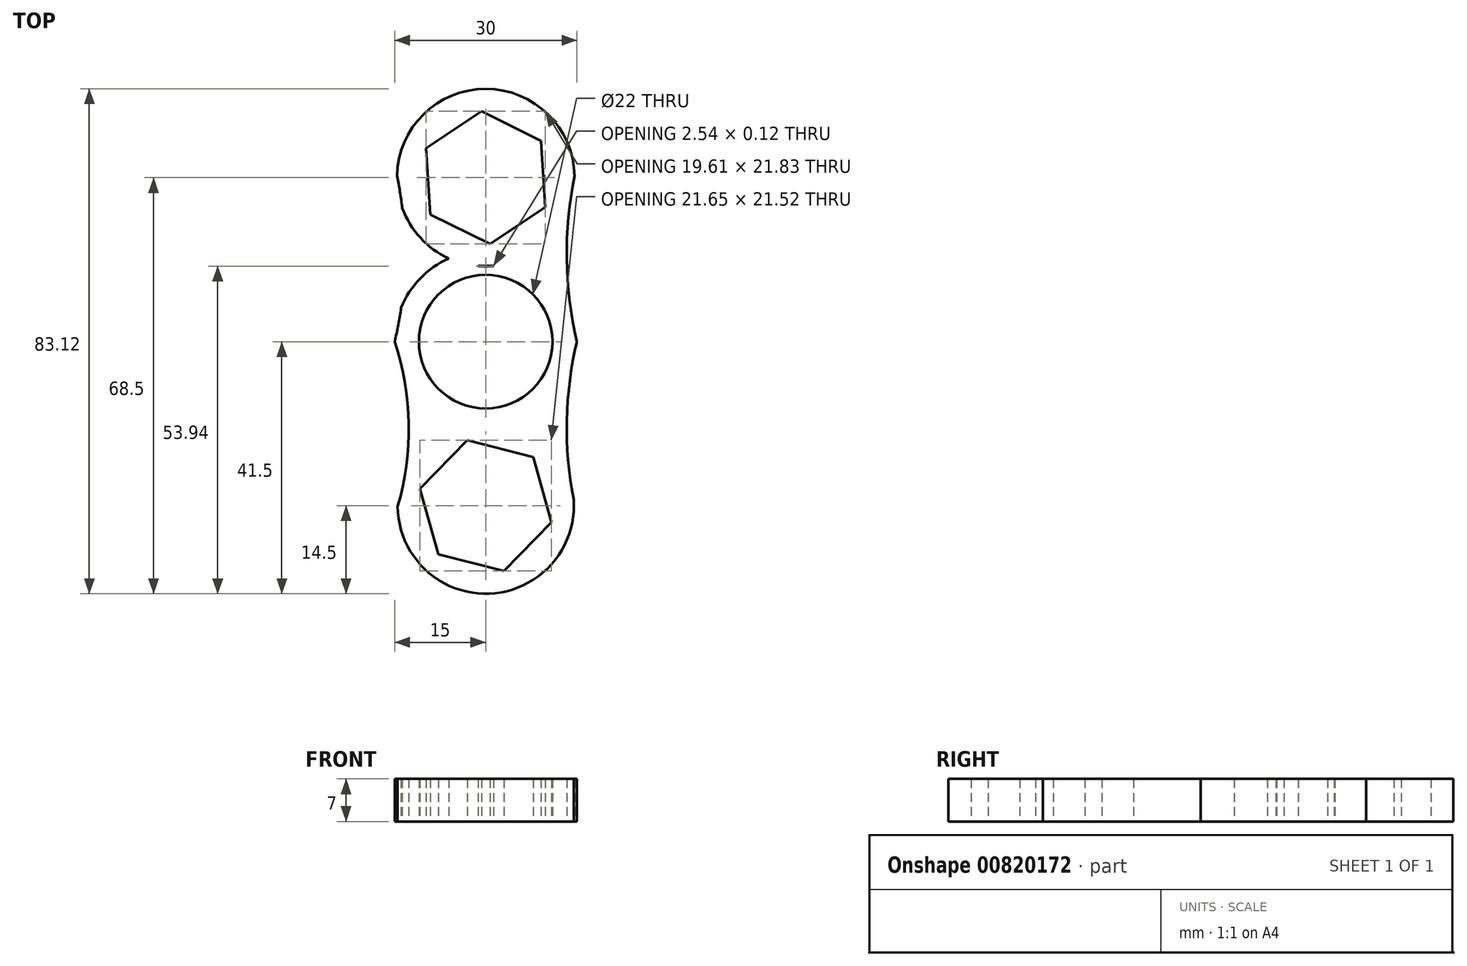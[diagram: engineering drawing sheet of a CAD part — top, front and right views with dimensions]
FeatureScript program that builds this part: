
annotation { "Feature Type Name" : "Feature", "Feature Type Description" : "" }
export const myFeature = defineFeature(function(context is Context, id is Id, definition is map)
    precondition{}
    {
        {
            var Q0;
            Q0=qCreatedBy(makeId("Top.planeOp"),FACE);
            var sketch = newSketch(context, id + "F0", { "sketchPlane" : qUnion([Q0])});
            skCircle(sketch, "E0", {"center": v(0, 0) * mm, "radius": 11 * mm});
            skCircle(sketch, "E1", {"center": v(0, 0) * mm, "radius": 12.5 * mm});
            skCircle(sketch, "E2", {"center": v(0, 27) * mm, "radius": 12 * mm});
            skCircle(sketch, "E3", {"center": v(0, -27) * mm, "radius": 12 * mm});
            skCircle(sketch, "E4", {"center": v(0, 27) * mm, "radius": 14.62 * mm});
            skCircle(sketch, "E5", {"center": v(0, 0) * mm, "radius": 15 * mm});
            skCircle(sketch, "E6", {"center": v(0, -27) * mm, "radius": 14.5 * mm});
            skCircle(sketch, "E7.cCircle", {"center": v(0, 27) * mm, "radius": 9.47 * mm, "construction": true});
            skLineSegment(sketch, "E7.0", {"start": v(9.8, 22.15) * mm, "end": v(0.7, 16.08) * mm});
            skLineSegment(sketch, "E7.1", {"start": v(0.7, 16.08) * mm, "end": v(-9.1, 20.94) * mm});
            skLineSegment(sketch, "E7.2", {"start": v(-9.1, 20.94) * mm, "end": v(-9.8, 31.85) * mm});
            skLineSegment(sketch, "E7.3", {"start": v(-9.8, 31.85) * mm, "end": v(-0.7, 37.92) * mm});
            skLineSegment(sketch, "E7.4", {"start": v(-0.7, 37.92) * mm, "end": v(9.1, 33.06) * mm});
            skLineSegment(sketch, "E7.5", {"start": v(9.1, 33.06) * mm, "end": v(9.8, 22.15) * mm});
            skPoint(sketch, "E7.0.midPoint", {"position": v(5.25, 19.11) * mm});
            skPoint(sketch, "E8.0.midPoint", {"position": v(5.25, -7.89) * mm});
            skCircle(sketch, "E9.cCircle", {"center": v(0, -27) * mm, "radius": 9.68 * mm, "construction": true});
            skLineSegment(sketch, "E9.0", {"start": v(10.82, -29.77) * mm, "end": v(3.01, -37.76) * mm});
            skLineSegment(sketch, "E9.1", {"start": v(3.01, -37.76) * mm, "end": v(-7.81, -34.99) * mm});
            skLineSegment(sketch, "E9.2", {"start": v(-7.81, -34.99) * mm, "end": v(-10.82, -24.23) * mm});
            skLineSegment(sketch, "E9.3", {"start": v(-10.82, -24.23) * mm, "end": v(-3.01, -16.24) * mm});
            skLineSegment(sketch, "E9.4", {"start": v(-3.01, -16.24) * mm, "end": v(7.81, -19.01) * mm});
            skLineSegment(sketch, "E9.5", {"start": v(7.81, -19.01) * mm, "end": v(10.82, -29.77) * mm});
            skPoint(sketch, "E9.0.midPoint", {"position": v(6.92, -33.77) * mm});
            skArc(sketch, "E10", {"start": v(15, 0) * mm, "mid": v(13.35, -12.96) * mm, "end": v(14.46, -25.98) * mm});
            skArc(sketch, "E11", {"start": v(14.62, 27.27) * mm, "mid": v(13.34, 13.62) * mm, "end": v(15, 0) * mm});
            skArc(sketch, "E12", {"start": v(-14.5, -27.14) * mm, "mid": v(-12.69, -13.53) * mm, "end": v(-15, 0) * mm});
            skArc(sketch, "E13", {"start": v(-15, 0) * mm, "mid": v(-13.29, 13.62) * mm, "end": v(-14.62, 27.3) * mm});
            skSolve(sketch);
        }
        {
            var Q0;
            {var subQ0=sQuery(id+"F0.wireOp",EDGE,"E3");Q0=makeQuery(id+"F0.imprint","IMPRINT",FACE,{"disambiguationData":[TD([[makeQuery(id+"F0.imprint","IMPRINT",EDGE,{"derivedFrom":subQ0}),-1.0]])]});}
            var Q1;
            {var subQ0=sQuery(id+"F0.wireOp",EDGE,"E4");var subQ1=sQuery(id+"F0.wireOp",EDGE,"E1");var subQ2=makeQuery(id+"F0.imprint","INTERSECT",VERTEX,{"disambiguationData":[OD(0.0)],"derivedFrom":[subQ1,subQ0]});Q1=makeQuery(id+"F0.imprint","IMPRINT",FACE,{"disambiguationData":[TD([[makeQuery(id+"F0.imprint","IMPRINT",EDGE,{"disambiguationData":[TD([[subQ2,-1.0]])],"derivedFrom":subQ1}),-1.0]])]});}
            var Q2;
            {var subQ0=sQuery(id+"F0.wireOp",EDGE,"E4");var subQ1=sQuery(id+"F0.wireOp",EDGE,"E1");var subQ2=makeQuery(id+"F0.imprint","INTERSECT",VERTEX,{"disambiguationData":[OD(1.0)],"derivedFrom":[subQ1,subQ0]});Q2=makeQuery(id+"F0.imprint","IMPRINT",FACE,{"disambiguationData":[TD([[makeQuery(id+"F0.imprint","IMPRINT",EDGE,{"disambiguationData":[TD([[subQ2,1.0]])],"derivedFrom":subQ1}),-1.0]])]});}
            var Q3;
            {var subQ0=sQuery(id+"F0.wireOp",EDGE,"E5");var subQ1=makeQuery(id+"F0.imprint","INTERSECT",VERTEX,{"derivedFrom":[sQuery(id+"F0.wireOp",EDGE,"E3"),subQ0]});Q3=makeQuery(id+"F0.imprint","IMPRINT",FACE,{"disambiguationData":[TD([[makeQuery(id+"F0.imprint","IMPRINT",EDGE,{"disambiguationData":[TD([[subQ1,1.0]])],"derivedFrom":subQ0}),1.0]])]});}
            var Q4;
            {var subQ2=sQuery(id+"F0.wireOp",EDGE,"E4");var subQ4=sQuery(id+"F0.wireOp",EDGE,"E1");var subQ7=makeQuery(id+"F0.imprint","INTERSECT",VERTEX,{"disambiguationData":[OD(0.0)],"derivedFrom":[subQ4,subQ2]});Q4=makeQuery(id+"F0.imprint","IMPRINT",FACE,{"disambiguationData":[TD([[makeQuery(id+"F0.imprint","IMPRINT",EDGE,{"disambiguationData":[TD([[subQ7,1.0]])],"derivedFrom":subQ4}),-1.0]])]});}
            var Q5;
            {var subQ0=sQuery(id+"F0.wireOp",EDGE,"E2");Q5=makeQuery(id+"F0.imprint","IMPRINT",FACE,{"disambiguationData":[TD([[makeQuery(id+"F0.imprint","IMPRINT",EDGE,{"derivedFrom":subQ0}),-1.0]])]});}
            extrude(context, id + "F1", {"entities" : qUnion([Q0, Q1, Q2, Q3, Q4, Q5]), "depth" : 7 * mm, "offsetDistance" : 25 * mm});
        }
        {
            var Q0;
            Q0=makeQuery(id+"F0.imprint","IMPRINT",FACE,{"disambiguationData":[TD([[makeQuery(id+"F0.imprint","IMPRINT",EDGE,{"derivedFrom":sQuery(id+"F0.wireOp",EDGE,"E2")}),1.0]])]});
            var Q1;
            {var subQ7=sQuery(id+"F0.wireOp",EDGE,"E0");var subQ12=sQuery(id+"F0.wireOp",EDGE,"E8.3");var subQ13=makeQuery(id+"F0.imprint","INTERSECT",VERTEX,{"disambiguationData":[OD(0.0)],"derivedFrom":[subQ7,subQ12]});Q1=makeQuery(id+"F0.imprint","IMPRINT",FACE,{"disambiguationData":[TD([[makeQuery(id+"F0.imprint","IMPRINT",EDGE,{"disambiguationData":[TD([[subQ13,-1.0]])],"derivedFrom":subQ7}),-1.0]])]});}
            var Q2;
            Q2=makeQuery(id+"F0.imprint","IMPRINT",FACE,{"disambiguationData":[TD([[makeQuery(id+"F0.imprint","IMPRINT",EDGE,{"derivedFrom":sQuery(id+"F0.wireOp",EDGE,"E3")}),1.0]])]});
            extrude(context, id + "F2", {"entities" : qUnion([Q0, Q1, Q2]), "operationType" : NewBodyOperationType.ADD, "depth" : 7 * mm, "offsetDistance" : 25 * mm});
        }
        {
            var Q0;
            {var subQ0=sQuery(id+"F0.wireOp",EDGE,"E11");var subQ1=sQuery(id+"F0.wireOp",EDGE,"E4");var subQ2=makeQuery(id+"F0.imprint","INTERSECT",VERTEX,{"disambiguationData":[OD(1.0)],"derivedFrom":[subQ1,subQ0]});Q0=makeQuery(id+"F0.imprint","IMPRINT",FACE,{"disambiguationData":[TD([[makeQuery(id+"F0.imprint","IMPRINT",EDGE,{"disambiguationData":[TD([[subQ2,1.0]])],"derivedFrom":subQ1}),-1.0]])]});}
            var Q1;
            {var subQ0=sQuery(id+"F0.wireOp",EDGE,"E13");var subQ1=sQuery(id+"F0.wireOp",EDGE,"E4");var subQ2=makeQuery(id+"F0.imprint","INTERSECT",VERTEX,{"disambiguationData":[OD(1.0)],"derivedFrom":[subQ1,subQ0]});Q1=makeQuery(id+"F0.imprint","IMPRINT",FACE,{"disambiguationData":[TD([[makeQuery(id+"F0.imprint","IMPRINT",EDGE,{"disambiguationData":[TD([[subQ2,-1.0]])],"derivedFrom":subQ1}),-1.0]])]});}
            var Q2;
            {var subQ0=sQuery(id+"F0.wireOp",EDGE,"E12");var subQ1=sQuery(id+"F0.wireOp",EDGE,"E5");var subQ2=makeQuery(id+"F0.imprint","INTERSECT",VERTEX,{"derivedFrom":[subQ1,subQ0]});Q2=makeQuery(id+"F0.imprint","IMPRINT",FACE,{"disambiguationData":[TD([[makeQuery(id+"F0.imprint","IMPRINT",EDGE,{"disambiguationData":[TD([[subQ2,-1.0]])],"derivedFrom":subQ1}),-1.0]])]});}
            var Q3;
            {var subQ0=sQuery(id+"F0.wireOp",EDGE,"E10");var subQ1=sQuery(id+"F0.wireOp",EDGE,"E5");var subQ2=makeQuery(id+"F0.imprint","INTERSECT",VERTEX,{"derivedFrom":[subQ1,subQ0]});Q3=makeQuery(id+"F0.imprint","IMPRINT",FACE,{"disambiguationData":[TD([[makeQuery(id+"F0.imprint","IMPRINT",EDGE,{"disambiguationData":[TD([[subQ2,1.0]])],"derivedFrom":subQ1}),-1.0]])]});}
            extrude(context, id + "F3", {"entities" : qUnion([Q0, Q1, Q2, Q3]), "operationType" : NewBodyOperationType.ADD, "depth" : 7 * mm, "offsetDistance" : 25 * mm});
        }
    });
